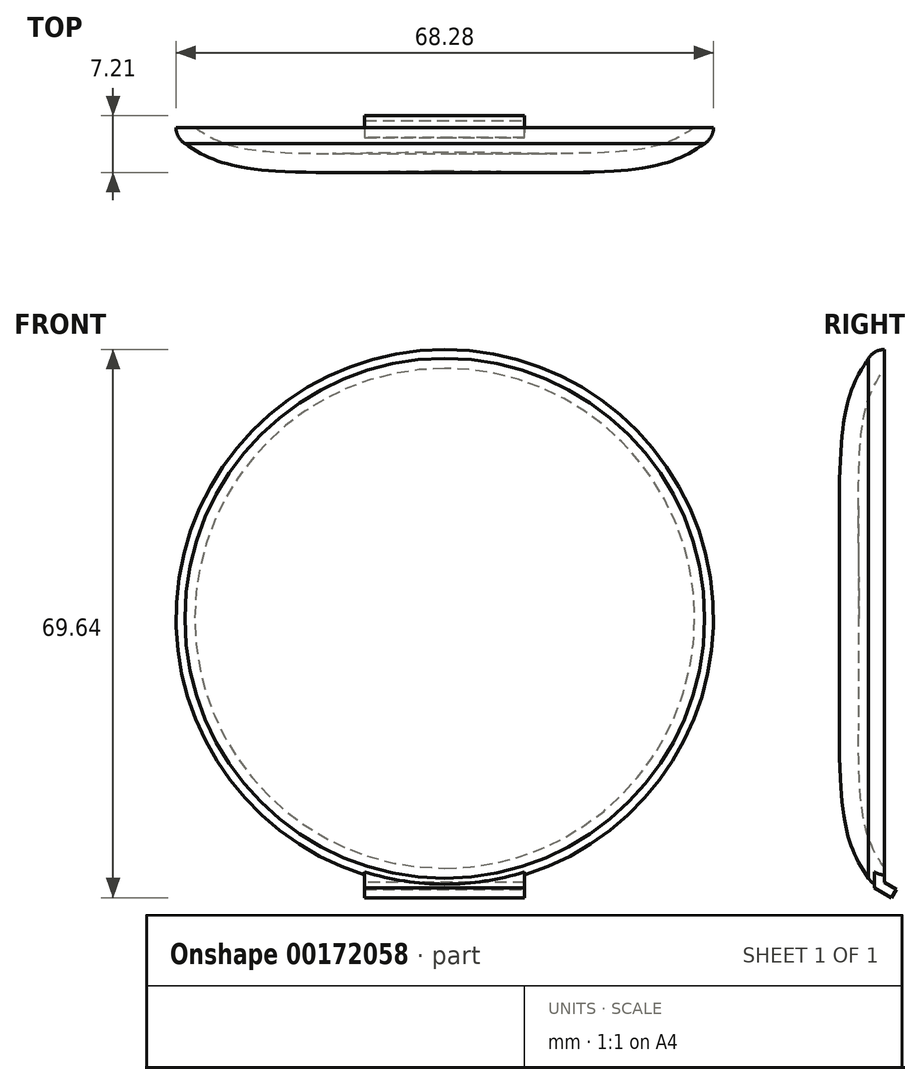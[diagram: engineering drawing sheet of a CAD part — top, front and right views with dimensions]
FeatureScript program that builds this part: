
annotation { "Feature Type Name" : "Feature", "Feature Type Description" : "" }
export const myFeature = defineFeature(function(context is Context, id is Id, definition is map)
    precondition{}
    {
        {
            var Q0;
            Q0=qCreatedBy(makeId("Right.planeOp"),FACE);
            var sketch = newSketch(context, id + "F0", { "sketchPlane" : qUnion([Q0])});
            skPoint(sketch, "E0", {"position": v(-3.18, 0) * mm});
            skFitSpline(sketch, "E1", {"points": [v(-3.18, 0) * mm, v(-2.44, 26.5) * mm, v(0, 31.75) * mm], "startDerivative": vector(0, 46.41) * mm, "endDerivative": vector(7.48, 11.96) * mm});
            skFitSpline(sketch, "E2.0", {"points": [v(-5.56, 0) * mm, v(-5.56, 1.92) * mm, v(-5.6, 5.76) * mm, v(-5.69, 11.37) * mm, v(-5.7, 16.65) * mm, v(-5.58, 20.62) * mm, v(-5.36, 23.48) * mm, v(-5.14, 25.12) * mm, v(-4.92, 26.35) * mm, v(-4.72, 27.23) * mm, v(-4.5, 28.05) * mm, v(-4.15, 29.07) * mm, v(-3.68, 30.2) * mm, v(-2.87, 31.7) * mm, v(-2.31, 32.56) * mm, v(-2.02, 33.02) * mm]});
            skLineSegment(sketch, "E3", {"start": v(-5.56, 0) * mm, "end": v(-3.18, 0) * mm});
            skArc(sketch, "E4", {"start": v(-2.02, 33.02) * mm, "mid": v(-1.16, 33.84) * mm, "end": v(0, 34.14) * mm});
            skLineSegment(sketch, "E5", {"start": v(0, 34.14) * mm, "end": v(0, 31.75) * mm});
            skSolve(sketch);
        }
        {
            var Q0;
            Q0 = qSketchRegion(id + "F0", true);
            var Q1;
            Q1=sQuery(id+"F0.wireOp",EDGE,"E3");
            revolve(context, id + "F1", {"entities" : qUnion([Q0]), "axis" : qUnion([Q1]), "revolveType" : RevolveType.FULL});
        }
        {
            var Q0;
            Q0=qCreatedBy(makeId("Front.planeOp"),FACE);
            var sketch = newSketch(context, id + "F2", { "sketchPlane" : qUnion([Q0])});
            skLineSegment(sketch, "E6", {"start": v(0, 0) * mm, "end": v(0, -87.95) * mm, "construction": true});
            skArc(sketch, "E7", {"start": v(10.16, -30.08) * mm, "mid": v(0, -31.75) * mm, "end": v(-10.16, -30.08) * mm});
            skLineSegment(sketch, "E8", {"start": v(10.16, -30.08) * mm, "end": v(10.16, -34.27) * mm});
            skLineSegment(sketch, "E9", {"start": v(10.16, -34.27) * mm, "end": v(-10.16, -34.27) * mm});
            skLineSegment(sketch, "E10", {"start": v(-10.16, -34.27) * mm, "end": v(-10.16, -30.08) * mm});
            skSolve(sketch);
        }
        {
            var Q0;
            Q0 = qSketchRegion(id + "F2", true);
            extrude(context, id + "F3", {"entities" : qUnion([Q0]), "operationType" : NewBodyOperationType.ADD, "depth" : 1.27 * mm});
        }
        {
            var Q0;
            Q0=makeQuery(id+"F3.opExtrude","SWEPT_FACE",FACE,{"disambiguationData":[OSD([sQuery(id+"F2.wireOp",EDGE,"E8")])]});
            var sketch = newSketch(context, id + "F4", { "sketchPlane" : qUnion([Q0])});
            skLineSegment(sketch, "E11", {"start": v(-1.27, -34.27) * mm, "end": v(-0.63, -33.17) * mm});
            skLineSegment(sketch, "E12", {"start": v(-0.64, -33.17) * mm, "end": v(1.5, -34.4) * mm});
            skLineSegment(sketch, "E13", {"start": v(1.5, -34.4) * mm, "end": v(0.86, -35.5) * mm});
            skLineSegment(sketch, "E14", {"start": v(0.86, -35.5) * mm, "end": v(-1.27, -34.27) * mm});
            skSolve(sketch);
        }
        {
            var Q0;
            Q0 = qSketchRegion(id + "F4", true);
            extrude(context, id + "F5", {"entities" : qUnion([Q0]), "operationType" : NewBodyOperationType.ADD, "oppositeDirection" : true, "depth" : 20.32 * mm});
        }
    });
